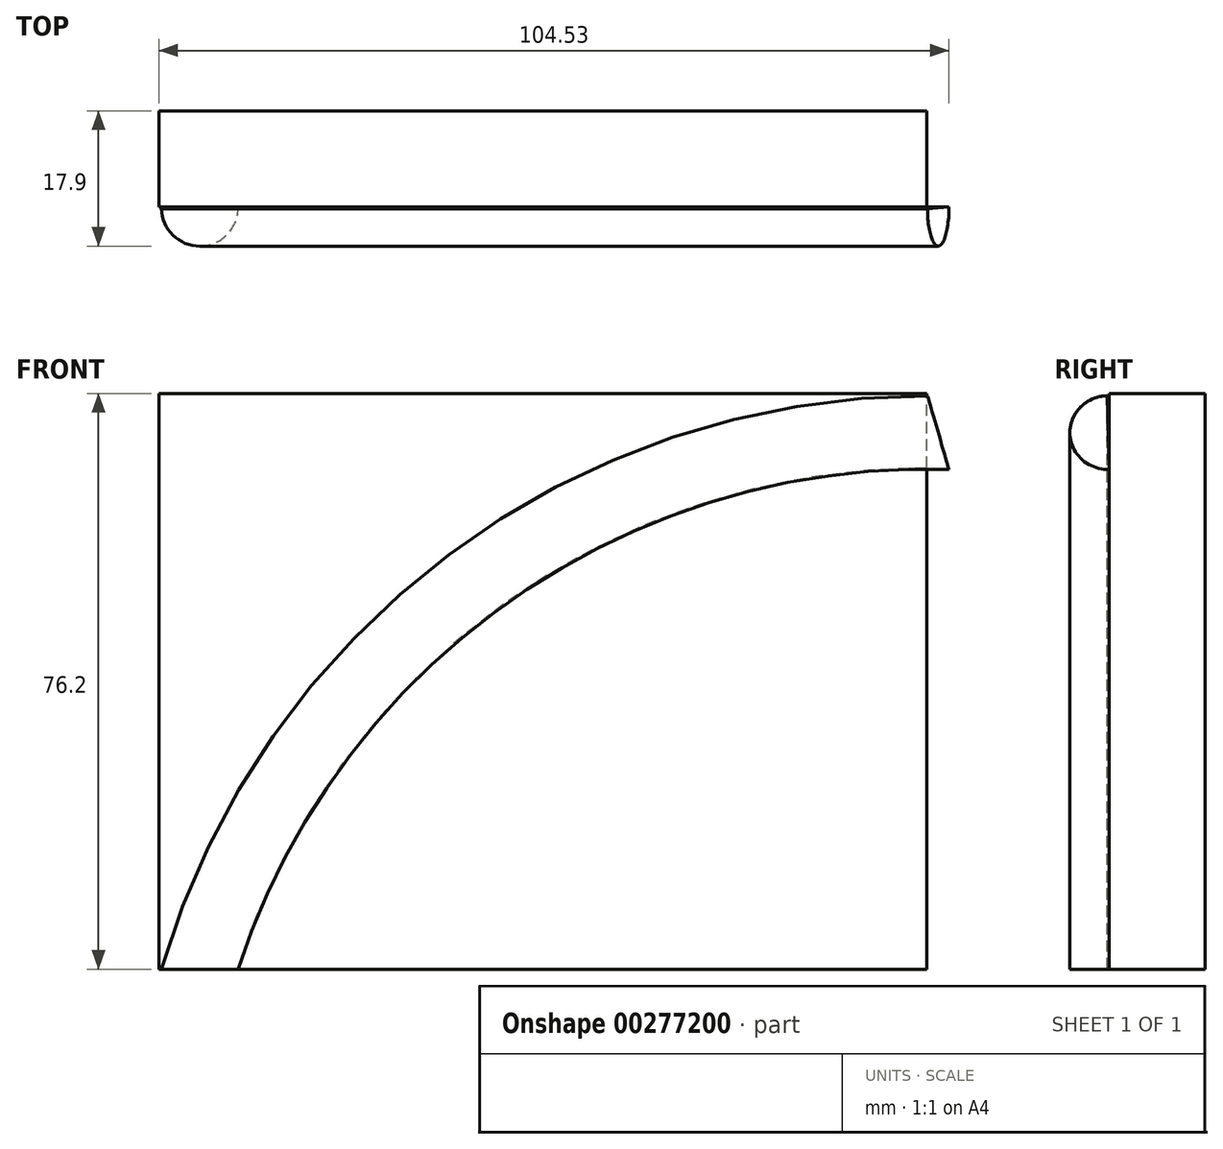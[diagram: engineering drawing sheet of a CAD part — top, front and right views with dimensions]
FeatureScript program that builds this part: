
annotation { "Feature Type Name" : "Feature", "Feature Type Description" : "" }
export const myFeature = defineFeature(function(context is Context, id is Id, definition is map)
    precondition{}
    {
        {
            var Q0;
            Q0=qCreatedBy(makeId("Front.planeOp"),FACE);
            var sketch = newSketch(context, id + "F0", { "sketchPlane" : qUnion([Q0])});
            skLineSegment(sketch, "E0.bottom", {"start": v(0, 0) * mm, "end": v(101.6, 0) * mm});
            skLineSegment(sketch, "E0.top", {"start": v(0, 76.2) * mm, "end": v(101.6, 76.2) * mm});
            skLineSegment(sketch, "E0.left", {"start": v(0, 0) * mm, "end": v(0, 76.2) * mm});
            skLineSegment(sketch, "E0.right", {"start": v(101.6, 0) * mm, "end": v(101.6, 76.2) * mm});
            skArc(sketch, "E1", {"start": v(101.6, 76.2) * mm, "mid": v(38.1, 55.03) * mm, "end": v(0, 0) * mm});
            skSolve(sketch);
        }
        {
            var Q0;
            Q0=qCreatedBy(makeId("Top.planeOp"),FACE);
            var sketch = newSketch(context, id + "F1", { "sketchPlane" : qUnion([Q0])});
            skLineSegment(sketch, "E2", {"start": v(0, 0) * mm, "end": v(0.32, -12.95) * mm});
            skLineSegment(sketch, "E3", {"start": v(0.32, -12.95) * mm, "end": v(10.48, -12.7) * mm});
            skArc(sketch, "E4", {"start": v(0.32, -12.95) * mm, "mid": v(5.53, -17.9) * mm, "end": v(10.48, -12.7) * mm});
            skSolve(sketch);
        }
        {
            var Q0;
            Q0=makeQuery(id+"F1.imprint","IMPRINT",FACE,{"disambiguationData":[TD([[makeQuery(id+"F1.imprint","IMPRINT",EDGE,{"derivedFrom":sQuery(id+"F1.wireOp",EDGE,"E3")}),-1.0]])]});
            var Q1;
            Q1=sQuery(id+"F0.wireOp",EDGE,"E1");
            sweep(context, id + "F2", {"profiles" : qUnion([Q0]), "path" : qUnion([Q1])});
        }
        {
            var Q0;
            Q0 = qSketchRegion(id + "F0", true);
            extrude(context, id + "F3", {"entities" : qUnion([Q0]), "operationType" : NewBodyOperationType.ADD, "depth" : 12.7 * mm});
        }
    });
